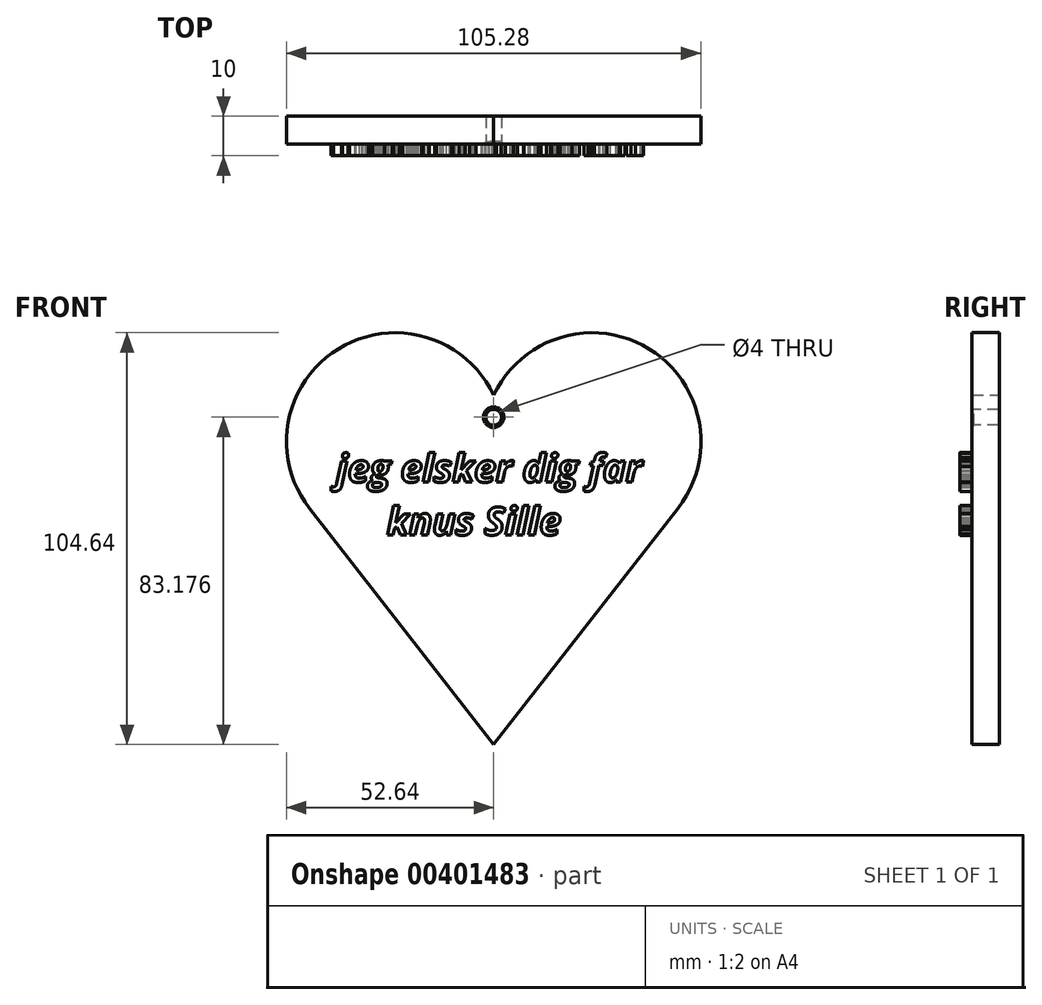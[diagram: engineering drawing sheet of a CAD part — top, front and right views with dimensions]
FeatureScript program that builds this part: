
annotation { "Feature Type Name" : "Feature", "Feature Type Description" : "" }
export const myFeature = defineFeature(function(context is Context, id is Id, definition is map)
    precondition{}
    {
        {
            var Q0;
            Q0=qCreatedBy(makeId("Front.planeOp"),FACE);
            var sketch = newSketch(context, id + "F0", { "sketchPlane" : qUnion([Q0])});
            skArc(sketch, "E0", {"start": v(0, 28.8) * mm, "mid": v(-39.49, 40.54) * mm, "end": v(-46.8, 0) * mm});
            skLineSegment(sketch, "E1", {"start": v(-46.8, 0) * mm, "end": v(0, -60) * mm});
            skLineSegment(sketch, "E2", {"start": v(0, -60) * mm, "end": v(46.8, 0) * mm});
            skArc(sketch, "E3", {"start": v(46.8, 0) * mm, "mid": v(39.49, 40.54) * mm, "end": v(0, 28.8) * mm});
            skSolve(sketch);
        }
        {
            var Q0;
            Q0 = qSketchRegion(id + "F0", true);
            extrude(context, id + "F1", {"entities" : qUnion([Q0]), "depth" : 7 * mm, "offsetDistance" : 25 * mm});
        }
        {
            var Q0;
            Q0=makeQuery(id+"F1.opExtrude","CAP_FACE",FACE,{"disambiguationData":[OSD([sQuery(id+"F0.wireOp",EDGE,"E0"),sQuery(id+"F0.wireOp",EDGE,"E1"),sQuery(id+"F0.wireOp",EDGE,"E2"),sQuery(id+"F0.wireOp",EDGE,"E3")])],"isStart":false});
            var sketch = newSketch(context, id + "F2", { "sketchPlane" : qUnion([Q0])});
            skText(sketch, "E4", { "text": "jeg elsker dig far \n     knus Sille", "fontName": "OpenSans-BoldItalic.ttf"});
            const initialGuessF2  = {"E4": [-0.04, 0.00668, 1, 0, 0.00711]};
            skSetInitialGuess(sketch, initialGuessF2);
            skSolve(sketch);
        }
        {
            var Q0;
            Q0=makeQuery(id+"F2.imprint","IMPRINT",FACE,{"disambiguationData":[TD([[makeQuery(id+"F2.imprint","IMPRINT",EDGE,{"derivedFrom":sQuery(id+"F2.wireOp",EDGE,"E4.sketch_text.stroke-0")}),1.0]])]});
            var sketch = newSketch(context, id + "F3", { "sketchPlane" : qUnion([Q0])});
            skSolve(sketch);
        }
        {
            var Q0;
            Q0 = qSketchRegion(id + "F2", true);
            extrude(context, id + "F4", {"entities" : qUnion([Q0]), "operationType" : NewBodyOperationType.ADD, "depth" : 3 * mm, "offsetDistance" : 25 * mm});
        }
        {
            var Q0;
            Q0=makeQuery(id+"F3.imprint","IMPRINT",FACE,{"disambiguationData":[TD([[makeQuery(id+"F3.imprint","IMPRINT",EDGE,{"derivedFrom":makeQuery(id+"F2.imprint","IMPRINT",EDGE,{"derivedFrom":sQuery(id+"F2.wireOp",EDGE,"E4.sketch_text.stroke-0")})}),1.0]])]});
            var sketch = newSketch(context, id + "F5", { "sketchPlane" : qUnion([Q0])});
            skPoint(sketch, "E5", {"position": v(0, 23.18) * mm});
            skSolve(sketch);
        }
        {
            var Q0;
            Q0=sQuery(id+"F5.wireOp",VERTEX,"E5");
            var Q1;
            Q1=makeQuery(id+"F1.opExtrude","SWEPT_BODY",BODY,{"disambiguationData":[OSD([sQuery(id+"F0.wireOp",EDGE,"E0"),sQuery(id+"F0.wireOp",EDGE,"E1"),sQuery(id+"F0.wireOp",EDGE,"E2"),sQuery(id+"F0.wireOp",EDGE,"E3")])]});
            hole(context, id + "F6", {"style" : HoleStyle.C_SINK, "endStyle" : HoleEndStyle.BLIND, "holeDiameter" : 4 * mm, "cSinkDiameter" : 5.2 * mm, "cSinkAngle" : 90 * degree, "majorDiameter" : 5 * mm, "holeDepth" : 60 * mm, "isTappedThrough" : true, "tappedDepth" : 12 * mm, "tapClearance" : 3, "startFromSketch" : true, "locations" : qUnion([Q0]), "scope" : qUnion([Q1])});
        }
    });
